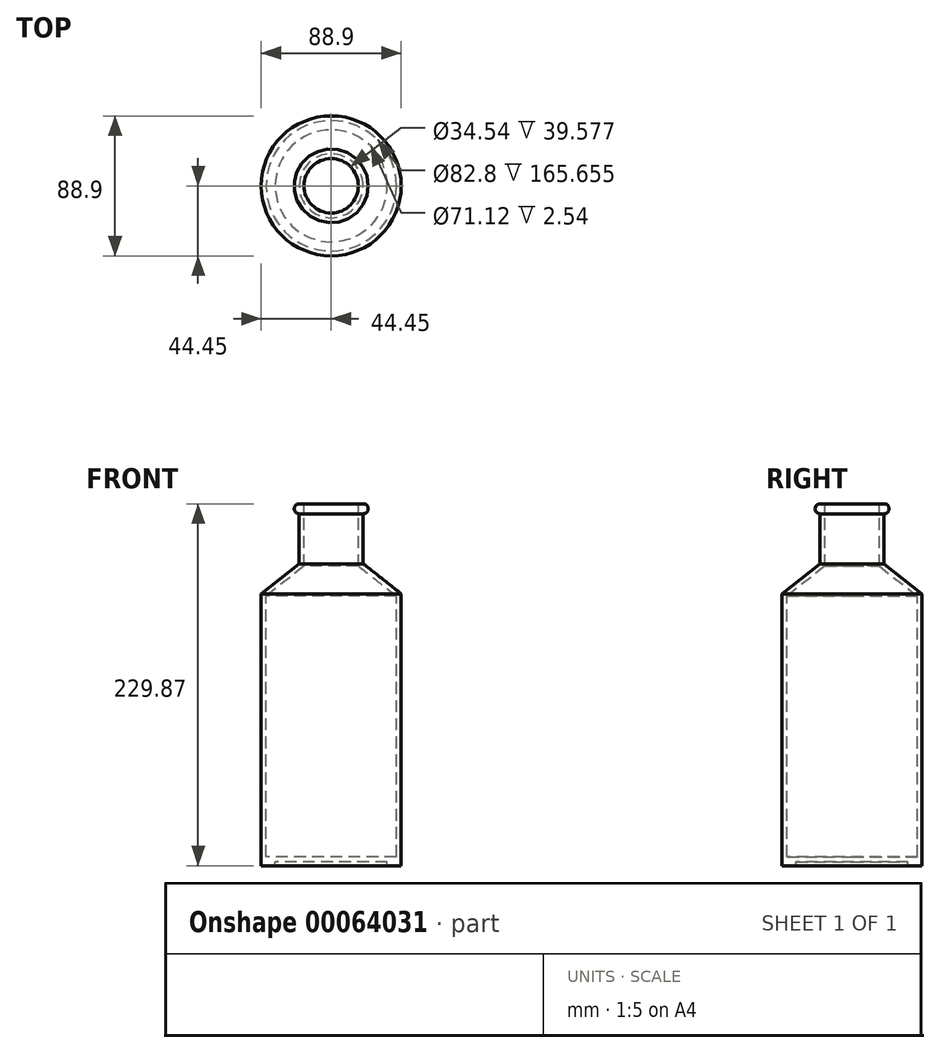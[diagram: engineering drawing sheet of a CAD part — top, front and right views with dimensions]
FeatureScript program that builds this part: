
annotation { "Feature Type Name" : "Feature", "Feature Type Description" : "" }
export const myFeature = defineFeature(function(context is Context, id is Id, definition is map)
    precondition{}
    {
        {
            var Q0;
            Q0=qCreatedBy(makeId("Front.planeOp"),FACE);
            var sketch = newSketch(context, id + "F0", { "sketchPlane" : qUnion([Q0])});
            skLineSegment(sketch, "E0.bottom", {"start": v(0, 0) * mm, "end": v(44.45, 0) * mm, "construction": true});
            skLineSegment(sketch, "E0.top", {"start": v(0, 172.72) * mm, "end": v(44.45, 172.72) * mm, "construction": true});
            skLineSegment(sketch, "E0.left", {"start": v(0, 0) * mm, "end": v(0, 172.72) * mm, "construction": true});
            skLineSegment(sketch, "E0.right", {"start": v(44.45, 0) * mm, "end": v(44.45, 172.72) * mm});
            skLineSegment(sketch, "E1", {"start": v(44.45, 172.72) * mm, "end": v(20.32, 191.77) * mm});
            skLineSegment(sketch, "E2", {"start": v(20.32, 191.77) * mm, "end": v(20.32, 223.52) * mm});
            skLineSegment(sketch, "E3", {"start": v(20.32, 223.52) * mm, "end": v(0, 223.52) * mm, "construction": true});
            skLineSegment(sketch, "E4", {"start": v(0, 223.52) * mm, "end": v(0, 172.72) * mm, "construction": true});
            skLineSegment(sketch, "E5", {"start": v(35.56, 0) * mm, "end": v(35.56, 2.54) * mm});
            skLineSegment(sketch, "E6", {"start": v(35.56, 2.54) * mm, "end": v(0, 2.54) * mm});
            skLineSegment(sketch, "E7", {"start": v(0, 229.87) * mm, "end": v(20.32, 229.87) * mm, "construction": true});
            skArc(sketch, "E8", {"start": v(20.32, 229.87) * mm, "mid": v(23.5, 226.7) * mm, "end": v(20.32, 223.52) * mm});
            skLineSegment(sketch, "E9", {"start": v(0, 229.87) * mm, "end": v(0, 0) * mm, "construction": true});
            skLineSegment(sketch, "E10", {"start": v(35.56, 0) * mm, "end": v(44.45, 0) * mm});
            skLineSegment(sketch, "E11.0", {"start": v(41.4, 5.59) * mm, "end": v(0, 5.59) * mm});
            skLineSegment(sketch, "E11.1", {"start": v(0, 226.82) * mm, "end": v(17.27, 226.82) * mm, "construction": true});
            skLineSegment(sketch, "E11.2", {"start": v(17.27, 190.3) * mm, "end": v(17.27, 226.82) * mm});
            skLineSegment(sketch, "E11.3", {"start": v(41.4, 171.24) * mm, "end": v(17.27, 190.3) * mm});
            skLineSegment(sketch, "E11.4", {"start": v(41.4, 5.59) * mm, "end": v(41.4, 171.24) * mm});
            skLineSegment(sketch, "E12", {"start": v(17.27, 226.82) * mm, "end": v(17.27, 229.87) * mm});
            skLineSegment(sketch, "E13", {"start": v(20.32, 229.87) * mm, "end": v(17.27, 229.87) * mm, "construction": true});
            skLineSegment(sketch, "E14", {"start": v(17.27, 229.87) * mm, "end": v(20.32, 229.87) * mm});
            skLineSegment(sketch, "E15", {"start": v(0, 5.59) * mm, "end": v(0, 2.54) * mm});
            skSolve(sketch);
        }
        {
            var Q0;
            Q0=makeQuery(id+"F0.imprint","IMPRINT",FACE,{"disambiguationData":[TD([[makeQuery(id+"F0.imprint","IMPRINT",EDGE,{"derivedFrom":sQuery(id+"F0.wireOp",EDGE,"E0.right")}),1.0]])]});
            var Q1;
            Q1=sQuery(id+"F0.wireOp",EDGE,"E9");
            revolve(context, id + "F1", {"entities" : qUnion([Q0]), "axis" : qUnion([Q1]), "revolveType" : RevolveType.FULL});
        }
    });
